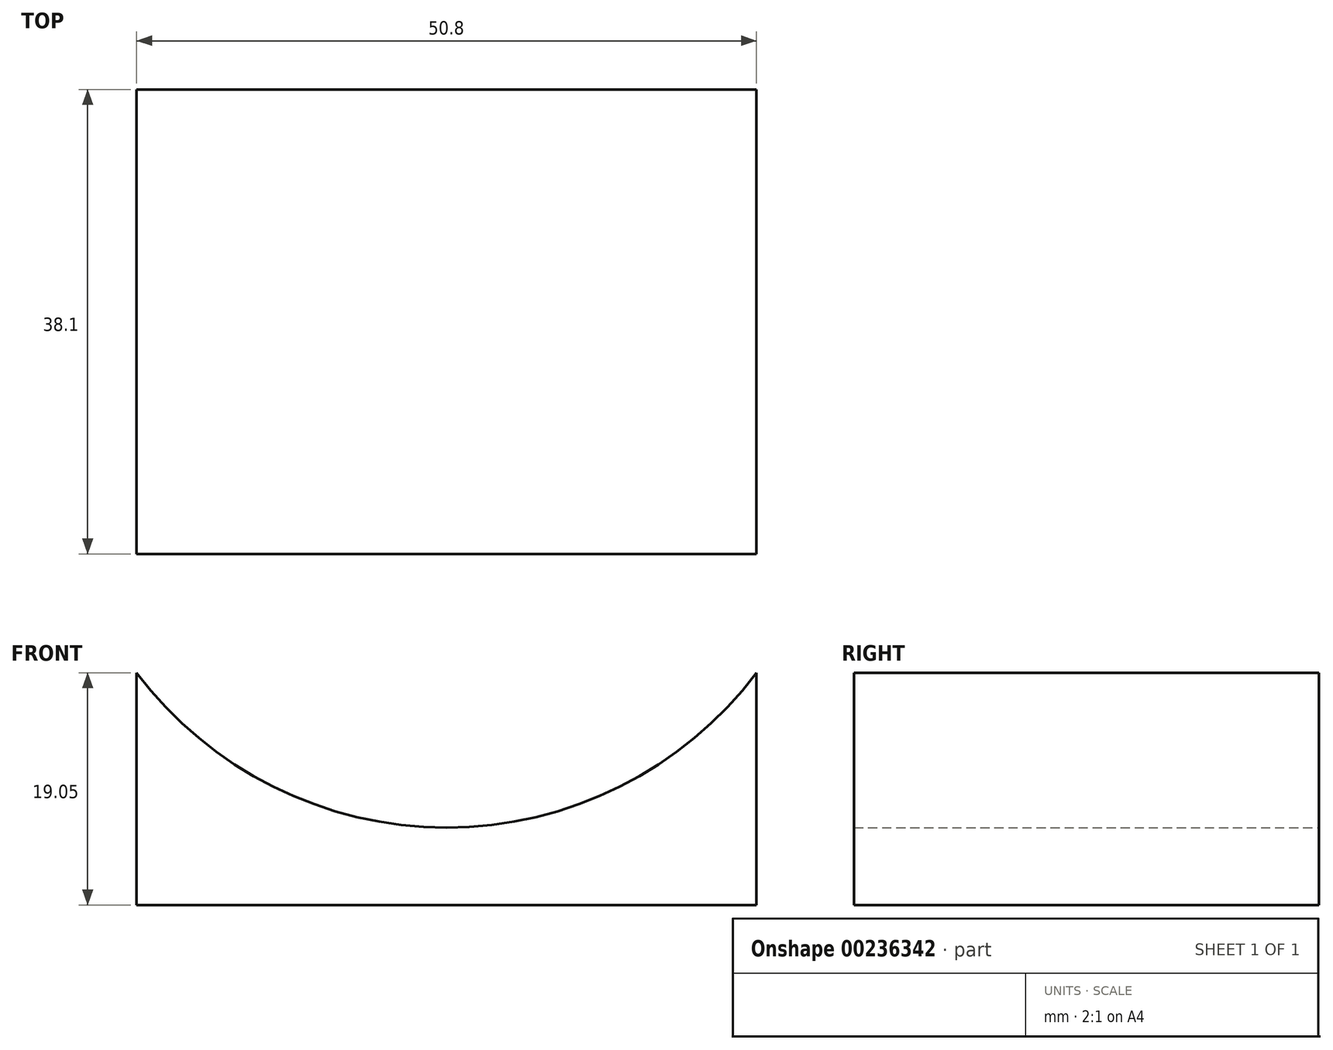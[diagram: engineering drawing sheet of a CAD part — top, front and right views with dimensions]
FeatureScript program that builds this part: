
annotation { "Feature Type Name" : "Feature", "Feature Type Description" : "" }
export const myFeature = defineFeature(function(context is Context, id is Id, definition is map)
    precondition{}
    {
        {
            var Q0;
            Q0=qCreatedBy(makeId("Front.planeOp"),FACE);
            var sketch = newSketch(context, id + "F0", { "sketchPlane" : qUnion([Q0])});
            skLineSegment(sketch, "E0", {"start": v(0, 0) * mm, "end": v(50.8, 0) * mm});
            skArc(sketch, "E1", {"start": v(0, 19.05) * mm, "mid": v(25.4, 6.35) * mm, "end": v(50.8, 19.05) * mm});
            skPoint(sketch, "E1.centerSnap0", {"position": v(25.4, 0) * mm});
            skLineSegment(sketch, "E2", {"start": v(0, 0) * mm, "end": v(0, 19.05) * mm});
            skLineSegment(sketch, "E3", {"start": v(50.8, 19.05) * mm, "end": v(50.8, 0) * mm});
            skSolve(sketch);
        }
        {
            var Q0;
            Q0 = qSketchRegion(id + "F0", true);
            extrude(context, id + "F1", {"entities" : qUnion([Q0]), "depth" : 38.1 * mm});
        }
    });
